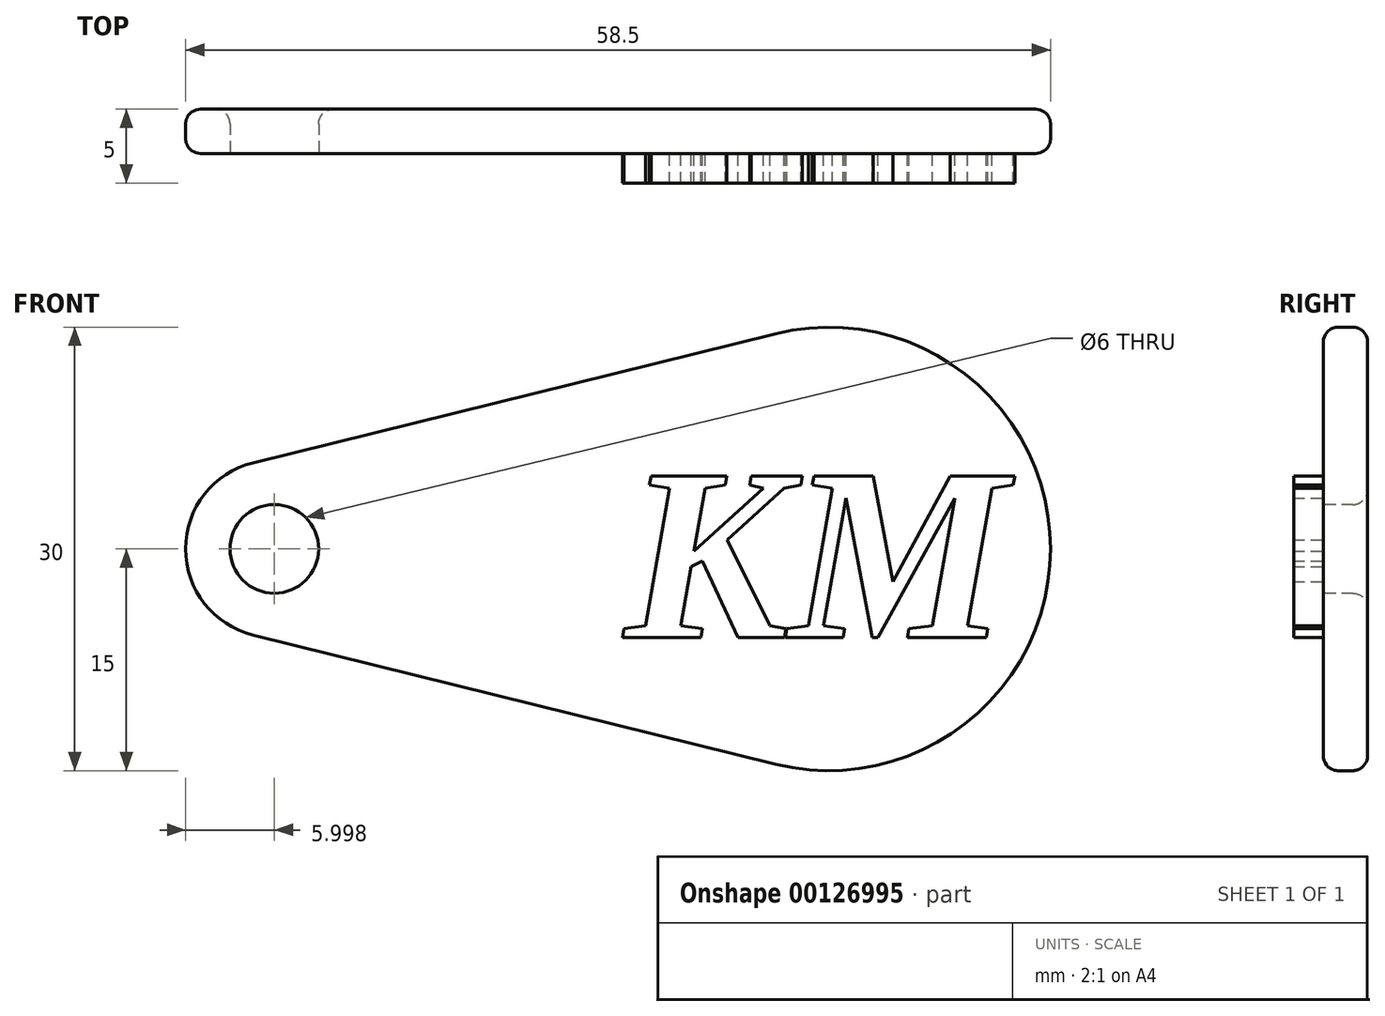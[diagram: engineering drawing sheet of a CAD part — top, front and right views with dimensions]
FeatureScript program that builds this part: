
annotation { "Feature Type Name" : "Feature", "Feature Type Description" : "" }
export const myFeature = defineFeature(function(context is Context, id is Id, definition is map)
    precondition{}
    {
        {
            var Q0;
            Q0=qCreatedBy(makeId("Front.planeOp"),FACE);
            var sketch = newSketch(context, id + "F0", { "sketchPlane" : qUnion([Q0])});
            skCircle(sketch, "E0", {"center": v(8.37, 0) * mm, "radius": 6 * mm});
            skCircle(sketch, "E1", {"center": v(45.87, 0) * mm, "radius": 15 * mm});
            skLineSegment(sketch, "E2", {"start": v(6.93, 5.82) * mm, "end": v(42.27, 14.56) * mm});
            skLineSegment(sketch, "E3", {"start": v(6.93, -5.82) * mm, "end": v(42.27, -14.56) * mm});
            skSolve(sketch);
        }
        {
            var Q0;
            Q0 = qSketchRegion(id + "F0", true);
            extrude(context, id + "F1", {"entities" : qUnion([Q0]), "depth" : 3 * mm});
        }
        {
            var Q0;
            Q0=makeQuery(id+"F1.opExtrude","CAP_FACE",FACE,{"disambiguationData":[OSD([sQuery(id+"F0.wireOp",EDGE,"E0"),sQuery(id+"F0.wireOp",EDGE,"E1"),sQuery(id+"F0.wireOp",EDGE,"E2"),sQuery(id+"F0.wireOp",EDGE,"E3")])],"isStart":false});
            var sketch = newSketch(context, id + "F2", { "sketchPlane" : qUnion([Q0])});
            skText(sketch, "E4", { "text": "KM", "fontName": "Tinos-BoldItalic.ttf"});
            const initialGuessF2  = {"E4": [0.03205, -0.006, 1, 0, 0.012]};
            skSetInitialGuess(sketch, initialGuessF2);
            skSolve(sketch);
        }
        {
            var Q0;
            Q0 = qSketchRegion(id + "F2", true);
            extrude(context, id + "F3", {"entities" : qUnion([Q0]), "operationType" : NewBodyOperationType.ADD, "depth" : 2 * mm});
        }
        {
            var Q0;
            Q0=makeQuery(id+"F1.opExtrude","CAP_FACE",FACE,{"disambiguationData":[OSD([sQuery(id+"F0.wireOp",EDGE,"E0"),sQuery(id+"F0.wireOp",EDGE,"E1"),sQuery(id+"F0.wireOp",EDGE,"E2"),sQuery(id+"F0.wireOp",EDGE,"E3")])],"isStart":false});
            var sketch = newSketch(context, id + "F4", { "sketchPlane" : qUnion([Q0])});
            skCircle(sketch, "E5", {"center": v(8.37, 0) * mm, "radius": 3 * mm});
            skSolve(sketch);
        }
        {
            var Q0;
            Q0 = qSketchRegion(id + "F4", true);
            extrude(context, id + "F5", {"entities" : qUnion([Q0]), "operationType" : NewBodyOperationType.REMOVE, "oppositeDirection" : true, "depth" : 25 * mm});
        }
        {
            var Q0;
            Q0=makeQuery(id+"F1.opExtrude","CAP_EDGE",EDGE,{"disambiguationData":[OSD([sQuery(id+"F0.wireOp",EDGE,"E2")])],"isStart":false});
            var Q1;
            Q1=makeQuery(id+"F5.boolean.opBoolean","COPY",EDGE,{"derivedFrom":makeQuery(id+"F5.opExtrude","CAP_EDGE",EDGE,{"disambiguationData":[OSD([sQuery(id+"F4.wireOp",EDGE,"E5")])],"isStart":true})});
            var Q2;
            Q2=makeQuery(id+"F1.opExtrude","CAP_EDGE",EDGE,{"disambiguationData":[OSD([sQuery(id+"F0.wireOp",EDGE,"E1")])],"isStart":true});
            var Q3;
            Q3=makeQuery(id+"F1.opExtrude","CAP_EDGE",EDGE,{"disambiguationData":[OSD([sQuery(id+"F0.wireOp",EDGE,"E3")])],"isStart":true});
            var Q4;
            Q4=makeQuery(id+"F1.opExtrude","CAP_EDGE",EDGE,{"disambiguationData":[OSD([sQuery(id+"F0.wireOp",EDGE,"E0")])],"isStart":true});
            var Q5;
            Q5=makeQuery(id+"F1.opExtrude","CAP_EDGE",EDGE,{"disambiguationData":[OSD([sQuery(id+"F0.wireOp",EDGE,"E1")])],"isStart":false});
            var Q6;
            Q6=makeQuery(id+"F1.opExtrude","CAP_EDGE",EDGE,{"disambiguationData":[OSD([sQuery(id+"F0.wireOp",EDGE,"E2")])],"isStart":true});
            var Q7;
            Q7=makeQuery(id+"F1.opExtrude","CAP_EDGE",EDGE,{"disambiguationData":[OSD([sQuery(id+"F0.wireOp",EDGE,"E3")])],"isStart":false});
            var Q8;
            Q8=makeQuery(id+"F1.opExtrude","CAP_EDGE",EDGE,{"disambiguationData":[OSD([sQuery(id+"F0.wireOp",EDGE,"E0")])],"isStart":false});
            var Q9;
            Q9=makeQuery(id+"F5.boolean.opBoolean","INTERSECT",EDGE,{"derivedFrom":[makeQuery(id+"F1.opExtrude","CAP_FACE",FACE,{"disambiguationData":[OSD([sQuery(id+"F0.wireOp",EDGE,"E0"),sQuery(id+"F0.wireOp",EDGE,"E1"),sQuery(id+"F0.wireOp",EDGE,"E2"),sQuery(id+"F0.wireOp",EDGE,"E3")])],"isStart":true}),makeQuery(id+"F5.opExtrude","SWEPT_FACE",FACE,{"disambiguationData":[OSD([sQuery(id+"F4.wireOp",EDGE,"E5")])]})]});
            fillet(context, id + "F6", {"entities" : qUnion([Q0, Q1, Q2, Q3, Q4, Q5, Q6, Q7, Q8, Q9]), "radius" : 1 * mm, "tangentPropagation" : true, "allowEdgeOverflow" : false});
        }
    });
